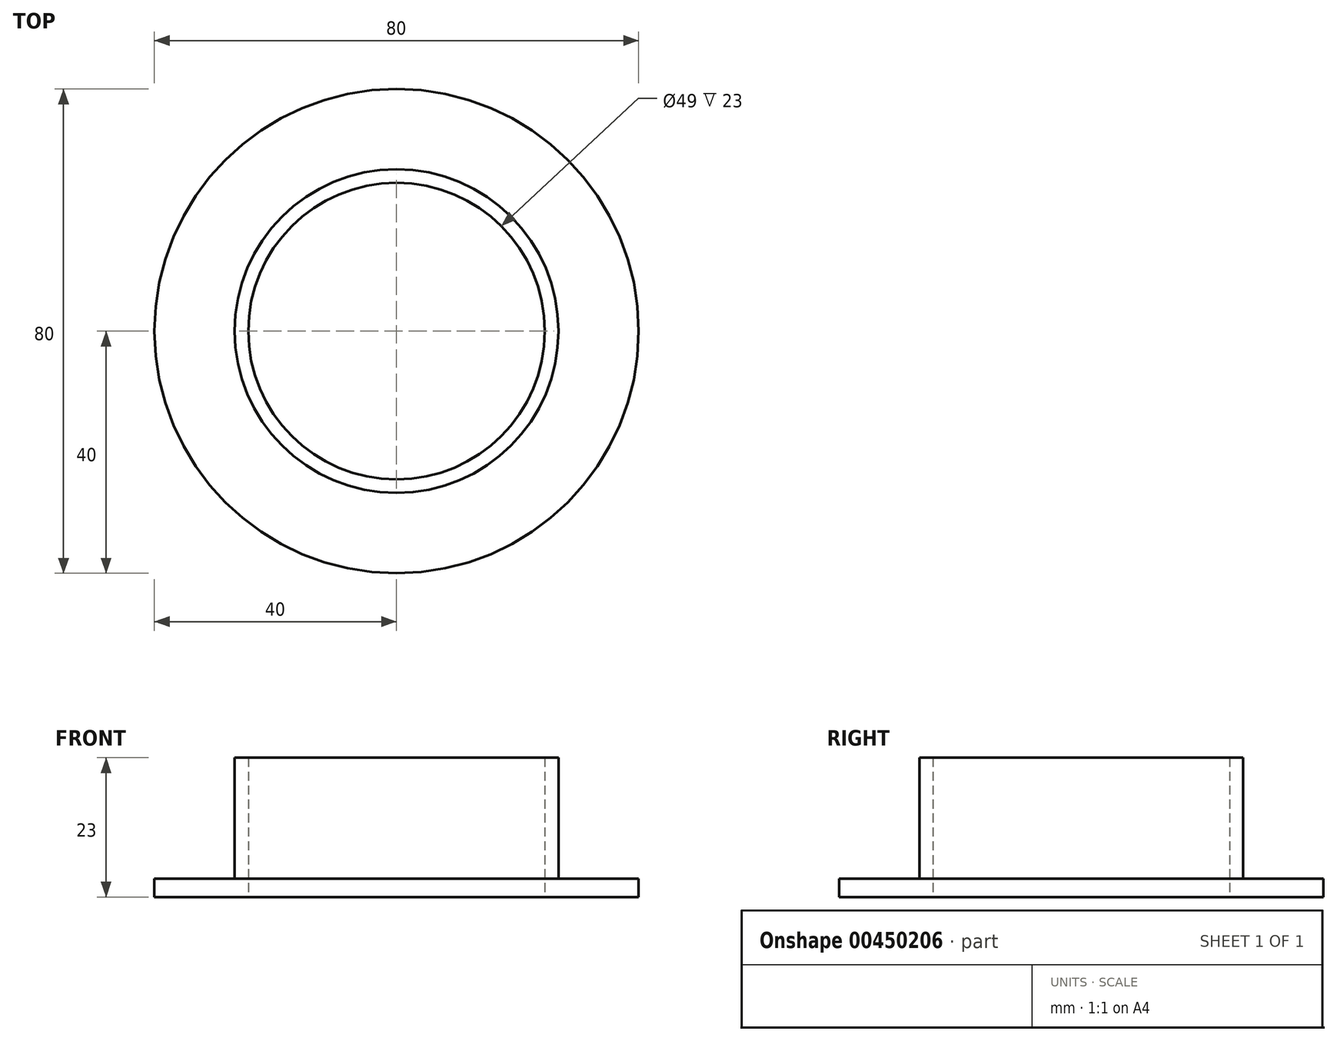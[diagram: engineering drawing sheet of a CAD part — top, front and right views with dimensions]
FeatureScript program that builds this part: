
annotation { "Feature Type Name" : "Feature", "Feature Type Description" : "" }
export const myFeature = defineFeature(function(context is Context, id is Id, definition is map)
    precondition{}
    {
        {
            var Q0;
            Q0=qCreatedBy(makeId("Top.planeOp"),FACE);
            var sketch = newSketch(context, id + "F0", { "sketchPlane" : qUnion([Q0])});
            skCircle(sketch, "E0", {"center": v(0, 0) * mm, "radius": 40 * mm});
            skSolve(sketch);
        }
        {
            var Q0;
            Q0 = qSketchRegion(id + "F0", true);
            extrude(context, id + "F1", {"entities" : qUnion([Q0]), "depth" : 3 * mm});
        }
        {
            var Q0;
            Q0=makeQuery(id+"F1.opExtrude","CAP_FACE",FACE,{"disambiguationData":[OSD([sQuery(id+"F0.wireOp",EDGE,"E0")])],"isStart":false});
            var sketch = newSketch(context, id + "F2", { "sketchPlane" : qUnion([Q0])});
            skCircle(sketch, "E1", {"center": v(0, 0) * mm, "radius": 26.75 * mm});
            skCircle(sketch, "E2", {"center": v(0, 0) * mm, "radius": 24.5 * mm});
            skSolve(sketch);
        }
        {
            var Q0;
            Q0 = qSketchRegion(id + "F2", true);
            extrude(context, id + "F3", {"entities" : qUnion([Q0]), "operationType" : NewBodyOperationType.ADD, "depth" : 20 * mm});
        }
        {
            var Q0;
            Q0=makeQuery(id+"F2.imprint","IMPRINT",FACE,{"disambiguationData":[TD([[makeQuery(id+"F2.imprint","IMPRINT",EDGE,{"derivedFrom":sQuery(id+"F2.wireOp",EDGE,"E2")}),1.0]])]});
            extrude(context, id + "F4", {"entities" : qUnion([Q0]), "operationType" : NewBodyOperationType.REMOVE, "endBound" : BoundingType.THROUGH_ALL, "oppositeDirection" : true, "depth" : 25 * mm});
        }
    });
